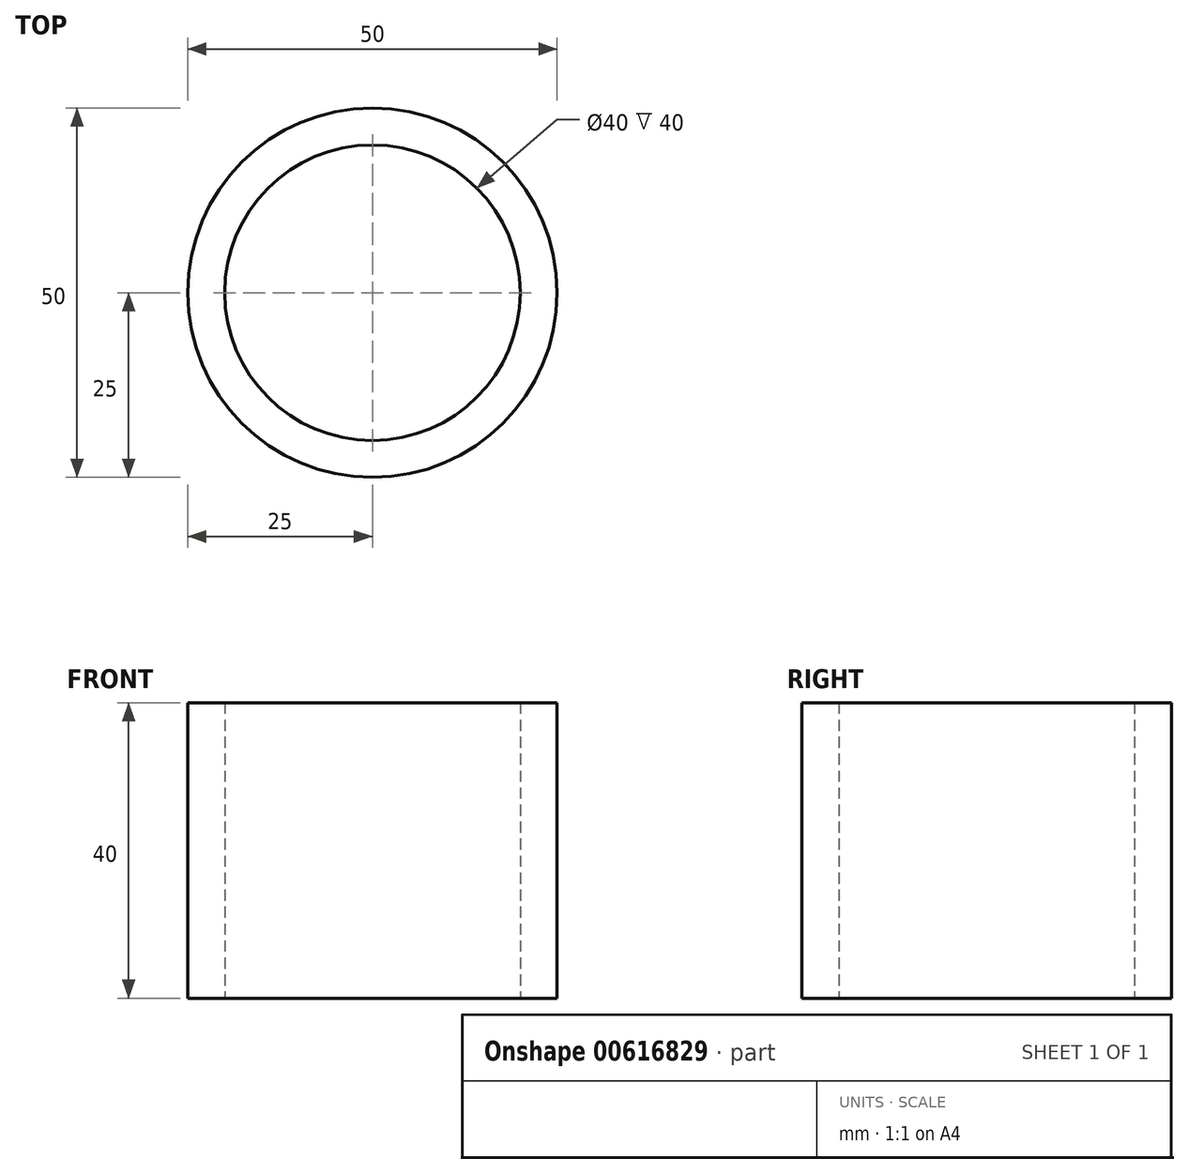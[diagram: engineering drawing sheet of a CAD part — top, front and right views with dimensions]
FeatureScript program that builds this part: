
annotation { "Feature Type Name" : "Feature", "Feature Type Description" : "" }
export const myFeature = defineFeature(function(context is Context, id is Id, definition is map)
    precondition{}
    {
        {
            var Q0;
            Q0=qCreatedBy(makeId("Top.planeOp"),FACE);
            var sketch = newSketch(context, id + "F0", { "sketchPlane" : qUnion([Q0])});
            skCircle(sketch, "E0", {"center": v(0, 0) * mm, "radius": 25 * mm});
            skCircle(sketch, "E1", {"center": v(0, 0) * mm, "radius": 20 * mm});
            skSolve(sketch);
        }
        {
            var Q0;
            Q0 = qSketchRegion(id + "F0", true);
            extrude(context, id + "F1", {"entities" : qUnion([Q0]), "depth" : 40 * mm, "offsetDistance" : 25 * mm});
        }
    });
